# Revit family: PRD_FrankeWS_MountingSupportForSquatPan_ZCMPX004
name_source: partatom
category: Plumbing Fixtures
revit_build: Autodesk Revit 2018 (Build: 20190510_1515(x64)
units: mm (PartAtom-declared; Revit-internal decimal feet)

## family parameters
Always vertical = Yes
Cut with Voids When Loaded = No
OmniClass Number = 23.45.05.14.99
OmniClass Title = Other Sanitary Washing Plumbing Fixtures
Part Type = Normal
Room Calculation Point = No
Round Connector Dimension = Use Diameter
Shared = Yes
Work Plane-Based = No

## types (1)
- ZCMPX004
    AssetType = Fixed
    BIMObjectName = PRD_AR_MountingSupportForSquatPan_ZCMPX004
    Category = Pr_20_85_47_47, Leg supports
    Description = Mounting support for squat pan, made of polystyrene with wall connection elements and fastening pins made of plastic and special installation foam for fast fixation on all surfaces.
    DimensionsHeight = 150 mm
    DurationUnit = year
    GrossWeight = 2.50 kg
    IfcExportAs = IfcBuildingElementProxy
    IfcExportType = NOTDEFINED
    Manufacturer = KWC Group AG
    ManufacturerName = KWC Group AG
    ManufacturerURL = www.kwc.com
    Model = ZCMPX004
    ModelNumber = 2000102731
    ModelReference = ZCMPX004
    MountingSupportMaterial = <By Category>
    NBSDescription = Leg supports
    NBSReference = 45-70-45/345
    Name = Mounting support for squat pan
    NetWeight = 2.20 kg
    NominalHeight = 150 mm
    NominalLength = 730 mm  [stored 2.39501 ft]
    NominalWidth = 730 mm  [stored 2.39501 ft]
    ProductInformation = https://pim.kwc.com
    Size = 730 x 150 x730 mm
    URL = www.kwc.com
    Uniclass2015Code = Pr_20_85_47_47
    Uniclass2015Title = Leg supports
    Uniclass2015Version = Products v1.7
    Version = 1
    WarrantyDurationUnit = year

note: [stored X ft] marks values corroborated as IEEE doubles in the binary element streams (Revit-internal decimal feet)

## geometry (parser evidence)
native form markers: Sweep x3
no freeform markers — native parametric forms only
